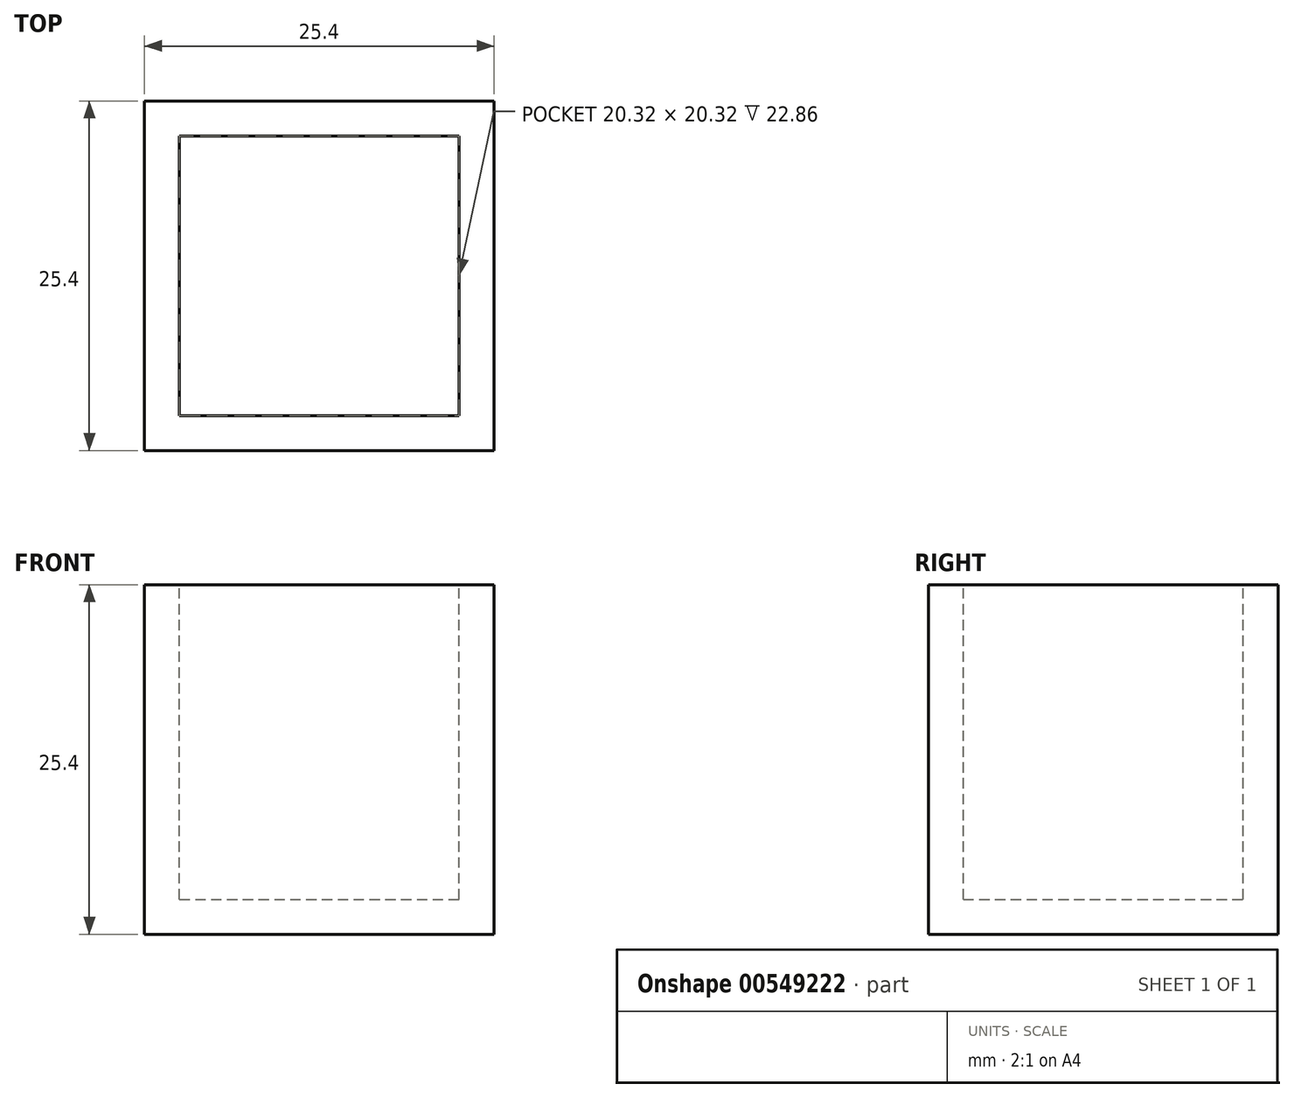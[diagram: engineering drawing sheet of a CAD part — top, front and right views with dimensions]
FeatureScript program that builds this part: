
annotation { "Feature Type Name" : "Feature", "Feature Type Description" : "" }
export const myFeature = defineFeature(function(context is Context, id is Id, definition is map)
    precondition{}
    {
        {
            var Q0;
            Q0=qCreatedBy(makeId("Front.planeOp"),FACE);
            var sketch = newSketch(context, id + "F0", { "sketchPlane" : qUnion([Q0])});
            skLineSegment(sketch, "E0.bottom", {"start": v(0, 0) * mm, "end": v(25.4, 0) * mm});
            skLineSegment(sketch, "E0.top", {"start": v(0, 25.4) * mm, "end": v(25.4, 25.4) * mm});
            skLineSegment(sketch, "E0.left", {"start": v(0, 0) * mm, "end": v(0, 25.4) * mm});
            skLineSegment(sketch, "E0.right", {"start": v(25.4, 0) * mm, "end": v(25.4, 25.4) * mm});
            skSolve(sketch);
        }
        {
            var Q0;
            Q0=qSketchRegion(id+"F0",true);
            extrude(context, id + "F1", {"entities" : qUnion([Q0]), "depth" : 25.4 * mm});
        }
        {
            var Q0;
            Q0=makeQuery(id+"F1.opExtrude","SWEPT_FACE",FACE,{"disambiguationData":[OSD([sQuery(id+"F0.wireOp",EDGE,"E0.top")])]});
            shell(context, id + "F2", {"entities" : qUnion([Q0]), "thickness" : 2.54 * mm});
        }
    });
